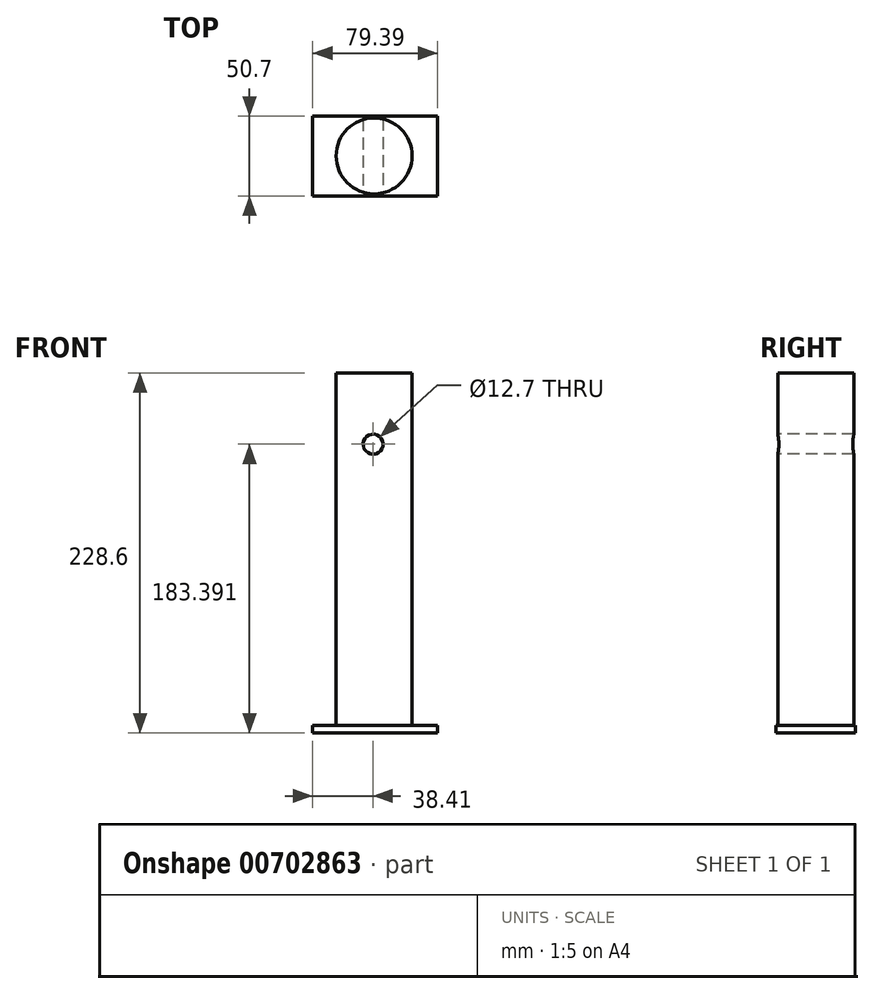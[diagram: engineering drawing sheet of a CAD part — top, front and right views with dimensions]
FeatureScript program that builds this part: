
annotation { "Feature Type Name" : "Feature", "Feature Type Description" : "" }
export const myFeature = defineFeature(function(context is Context, id is Id, definition is map)
    precondition{}
    {
        {
            var Q0;
            Q0=qCreatedBy(makeId("Top.planeOp"),FACE);
            var sketch = newSketch(context, id + "F0", { "sketchPlane" : qUnion([Q0])});
            skCircle(sketch, "E0", {"center": v(-7.29, 25.4) * mm, "radius": 24.13 * mm});
            skSolve(sketch);
        }
        {
            var Q0;
            Q0 = qSketchRegion(id + "F0", true);
            extrude(context, id + "F1", {"entities" : qUnion([Q0]), "depth" : 228.6 * mm, "offsetDistance" : 25.4 * mm});
        }
        {
            var Q0;
            Q0=qCreatedBy(makeId("Front.planeOp"),FACE);
            var sketch = newSketch(context, id + "F2", { "sketchPlane" : qUnion([Q0])});
            skCircle(sketch, "E1", {"center": v(-7.95, 183.4) * mm, "radius": 6.35 * mm});
            skSolve(sketch);
        }
        {
            var Q0;
            Q0 = qSketchRegion(id + "F2", true);
            extrude(context, id + "F3", {"entities" : qUnion([Q0]), "operationType" : NewBodyOperationType.REMOVE, "oppositeDirection" : true, "depth" : 66.3 * mm, "offsetDistance" : 25.4 * mm});
        }
        {
            var Q0;
            Q0=qCreatedBy(makeId("Top.planeOp"),FACE);
            var sketch = newSketch(context, id + "F4", { "sketchPlane" : qUnion([Q0])});
            skLineSegment(sketch, "E2.bottom", {"start": v(-46.36, 0) * mm, "end": v(33.03, 0) * mm});
            skLineSegment(sketch, "E2.top", {"start": v(-46.36, 50.7) * mm, "end": v(33.03, 50.7) * mm});
            skLineSegment(sketch, "E2.left", {"start": v(-46.36, 0) * mm, "end": v(-46.36, 50.7) * mm});
            skLineSegment(sketch, "E2.right", {"start": v(33.03, 0) * mm, "end": v(33.03, 50.7) * mm});
            skSolve(sketch);
        }
        {
            var Q0;
            Q0 = qSketchRegion(id + "F4", true);
            extrude(context, id + "F5", {"entities" : qUnion([Q0]), "operationType" : NewBodyOperationType.ADD, "depth" : 4.83 * mm, "offsetDistance" : 25.4 * mm});
        }
    });
